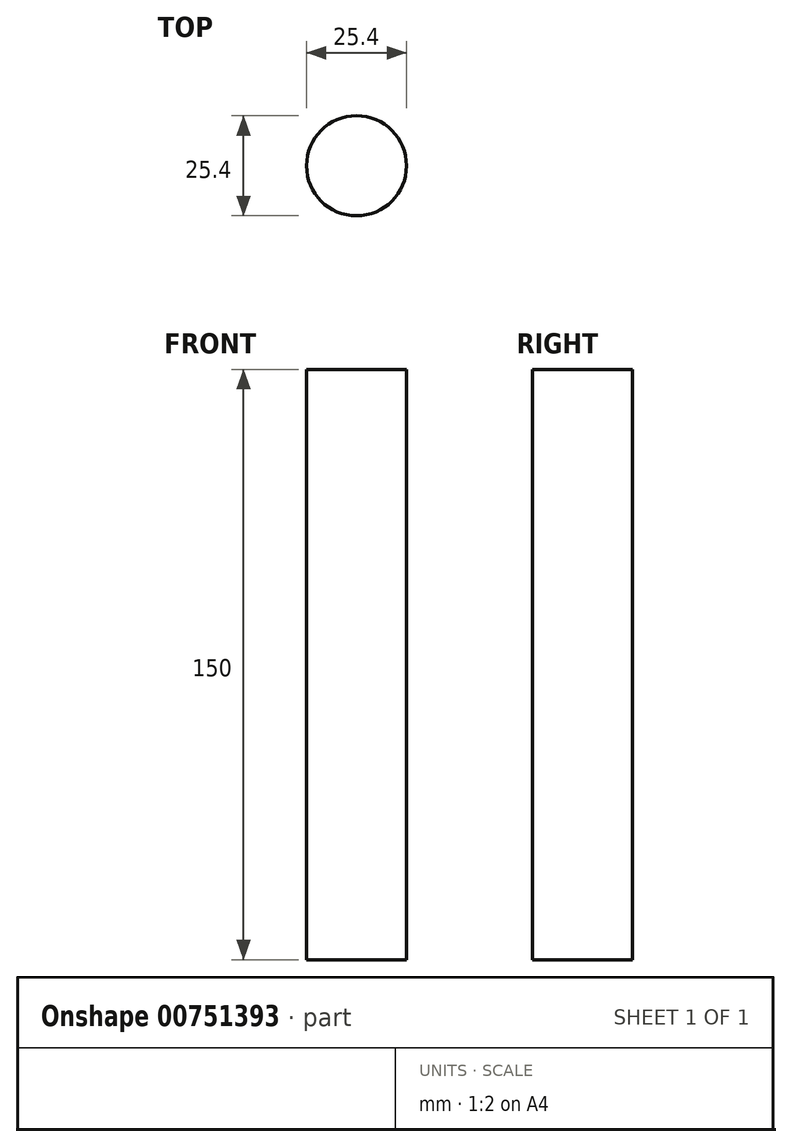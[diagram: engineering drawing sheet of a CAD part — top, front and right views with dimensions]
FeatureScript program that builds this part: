
annotation { "Feature Type Name" : "Feature", "Feature Type Description" : "" }
export const myFeature = defineFeature(function(context is Context, id is Id, definition is map)
    precondition{}
    {
        {
            var Q0;
            Q0=qCreatedBy(makeId("Top.planeOp"),FACE);
            var sketch = newSketch(context, id + "F0", { "sketchPlane" : qUnion([Q0])});
            skCircle(sketch, "E0", {"center": v(0, 0) * mm, "radius": 12.7 * mm});
            skSolve(sketch);
        }
        {
            var Q0;
            Q0=makeQuery(id+"F0.imprint","IMPRINT",FACE,{"disambiguationData":[TD([[makeQuery(id+"F0.imprint","IMPRINT",EDGE,{"derivedFrom":sQuery(id+"F0.wireOp",EDGE,"E0")}),1.0]])]});
            extrude(context, id + "F1", {"entities" : qUnion([Q0]), "depth" : 150 * mm, "offsetDistance" : 25 * mm});
        }
    });
